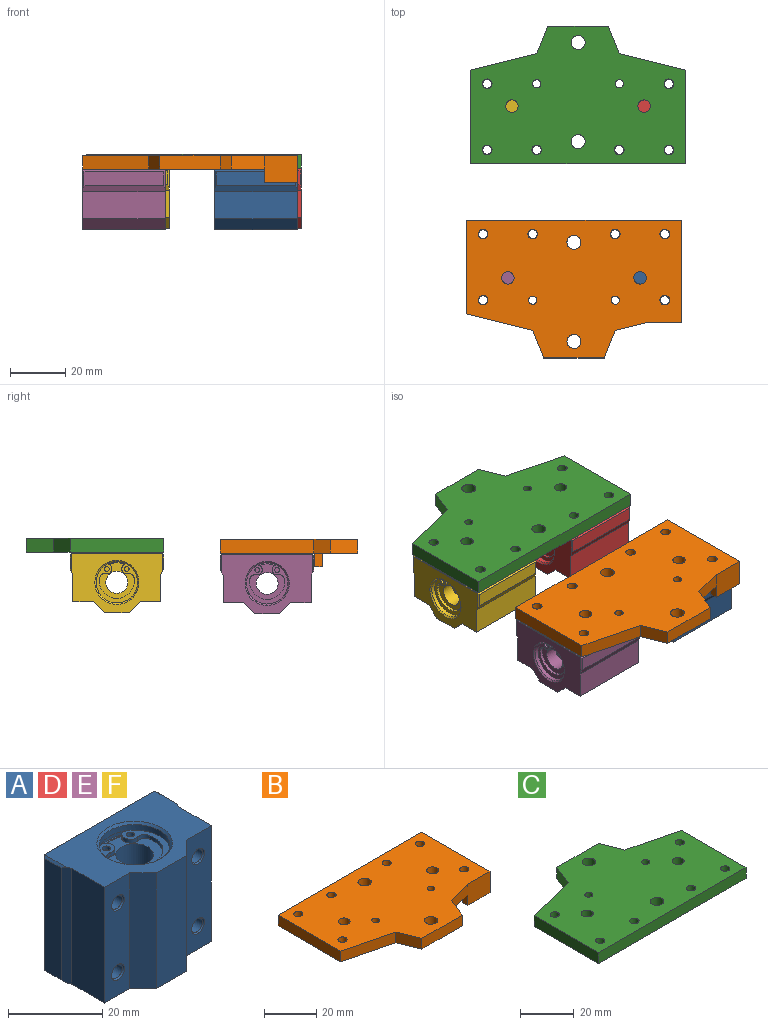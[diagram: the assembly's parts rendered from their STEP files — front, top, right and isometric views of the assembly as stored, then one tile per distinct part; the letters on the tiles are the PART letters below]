
ASSEMBLY  parts=6 mates=4
PART A: 101 faces, bbox 34x22x30 mm
  f0: cylinder r=7.5mm len=15mm, axis (0,0,-1), area 11.8mm2, adj f30,f89
  f1: plane 9.06x1.44mm, normal (0,0,-1), area 2.8mm2, adj f26,f27,f84,f85
  f2: plane 9.06x1.44mm, normal (0,0,1), area 2.8mm2, adj f31,f32,f70,f71
  f3: plane 30x7.5mm, normal (0,-1,0), area 201.6mm2, adj f7,f8,f11,f12,f52,f57
  f4: plane 29x8mm, normal (0,1,0), area 206.9mm2, adj f21,f22,f23,f24,f48,f53
  f5: plane 30x7.5mm, normal (0,-1,0), area 201.6mm2, adj f7,f8,f14,f15,f42,f47
  f6: plane 29x8mm, normal (0,1,0), area 206.9mm2, adj f18,f19,f23,f24,f38,f43
  f7: plane 33x21.5mm, normal (0,0,1), area 418mm2, adj f3,f5,f10,f11,f12,f13,f14,f15
  f8: plane 33x21.5mm, normal (0,0,-1), area 418mm2, adj f3,f5,f10,f11,f12,f13,f14,f15
  f9: plane 29x5mm, normal (-1,0,0), area 145mm2, adj f10,f22,f34,f35
  f10: plane 30x2.14mm, normal (-0.91,-0.42,0), area 70.4mm2, adj f7,f8,f9,f11,f34,f35
  f11: plane 30x9.86mm, normal (-1,0,0), area 295.7mm2, adj f3,f7,f8,f10
  f12: plane 30x4mm, normal (-0.71,-0.71,0), area 169.7mm2, adj f3,f7,f8,f13
  f13: plane 30x9mm, normal (0,-1,0), area 270mm2, adj f7,f8,f12,f14
  f14: plane 30x4mm, normal (0.71,-0.71,0), area 169.7mm2, adj f5,f7,f8,f13
  f15: plane 30x9.86mm, normal (1,0,0), area 295.7mm2, adj f5,f7,f8,f16
  f16: plane 30x2.14mm, normal (0.91,-0.42,0), area 70.4mm2, adj f7,f8,f15,f17,f36,f37
  f17: plane 29x5mm, normal (1,0,0), area 145mm2, adj f16,f18,f36,f37
  f18: plane 30x1mm, normal (0.71,0.71,0), area 41.7mm2, adj f6,f17,f23,f24,f36,f37
  f19: plane 29.8x0.4mm, normal (-0.71,0.71,0), area 16.6mm2, adj f6,f20,f23,f24
  f20: plane 29.8x15.2mm, normal (0,1,0), area 453mm2, adj f19,f21,f23,f24
  f21: plane 29.8x0.4mm, normal (0.71,0.71,0), area 16.6mm2, adj f4,f20,f23,f24
  f22: plane 30x1mm, normal (-0.71,0.71,0), area 41.7mm2, adj f4,f9,f23,f24,f34,f35
  f23: plane 33x0.5mm, normal (0,0.71,-0.71), area 14.2mm2, adj f4,f6,f8,f18,f19,f20,f21,f22
  f24: plane 33x0.5mm, normal (0,0.71,0.71), area 14.2mm2, adj f4,f6,f7,f18,f19,f20,f21,f22
  f25: cone r=8mm half-angle=45deg, axis (0,0,1), area 34.4mm2, adj f7,f26
  f26: cylinder r=7.5mm len=15mm, axis (0,0,-1), area 70.7mm2, adj f1,f25,f92
  f27: cylinder r=7.85mm len=15.7mm, axis (0,0,-1), area 17.1mm2, adj f1,f28,f84,f85,f86
  f28: plane 15.7x15.7mm, normal (0,0,1), area 16.9mm2, adj f27,f29
  f29: cylinder r=7.5mm len=15mm, axis (0,0,-1), area 11.8mm2, adj f28,f87
  f30: plane 15.7x15.7mm, normal (0,0,-1), area 16.9mm2, adj f0,f31
  f31: cylinder r=7.85mm len=15.7mm, axis (0,0,-1), area 17.1mm2, adj f2,f30,f70,f71,f72
  f32: cylinder r=7.5mm len=15mm, axis (0,0,-1), area 70.7mm2, adj f2,f33,f60
  f33: cone r=7.5mm half-angle=45deg, axis (0,0,-1), area 34.4mm2, adj f8,f32
  f34: plane 6.57x0.5mm, normal (-0.71,0,0.71), area 4.1mm2, adj f7,f9,f10,f22
  f35: plane 6.57x0.5mm, normal (-0.71,0,-0.71), area 4.1mm2, adj f8,f9,f10,f22
  f36: plane 6.57x0.5mm, normal (0.71,0,0.71), area 4.1mm2, adj f7,f16,f17,f18
  f37: plane 6.57x0.5mm, normal (0.71,0,-0.71), area 4.1mm2, adj f8,f16,f17,f18
  f38: cone r=2mm half-angle=45deg, axis (0,1,0), area 6.1mm2, adj f6,f39
  f39: cylinder r=1.62mm len=9.62mm, axis (0,-1,0), area 98mm2, adj f38,f40
  f40: plane 3.4x3.4mm, normal (0,-1,0), area 0.8mm2, adj f39,f41
  f41: cylinder r=1.7mm len=7.6mm, axis (0,-1,0), area 81.2mm2, adj f40,f42
  f42: cone r=1.7mm half-angle=30deg, axis (0,-1,0), area 5.3mm2, adj f5,f41
  f43: cone r=2mm half-angle=45deg, axis (0,1,0), area 6.1mm2, adj f6,f44
  f44: cylinder r=1.62mm len=9.62mm, axis (0,-1,0), area 98mm2, adj f43,f45
  f45: plane 3.4x3.4mm, normal (0,-1,0), area 0.8mm2, adj f44,f46
  f46: cylinder r=1.7mm len=7.6mm, axis (0,-1,0), area 81.2mm2, adj f45,f47
  f47: cone r=1.7mm half-angle=30deg, axis (0,-1,0), area 5.3mm2, adj f5,f46
  f48: cone r=2mm half-angle=45deg, axis (0,1,0), area 6.1mm2, adj f4,f49
  f49: cylinder r=1.62mm len=9.62mm, axis (0,-1,0), area 98mm2, adj f48,f50
  f50: plane 3.4x3.4mm, normal (0,-1,0), area 0.8mm2, adj f49,f51
  f51: cylinder r=1.7mm len=7.6mm, axis (0,-1,0), area 81.2mm2, adj f50,f52
  f52: cone r=1.7mm half-angle=30deg, axis (0,-1,0), area 5.3mm2, adj f3,f51
  f53: cone r=2mm half-angle=45deg, axis (0,1,0), area 6.1mm2, adj f4,f54
  f54: cylinder r=1.62mm len=9.62mm, axis (0,-1,0), area 98mm2, adj f53,f55
  f55: plane 3.4x3.4mm, normal (0,-1,0), area 0.8mm2, adj f54,f56
  f56: cylinder r=1.7mm len=7.6mm, axis (0,-1,0), area 81.2mm2, adj f55,f57
  f57: cone r=1.7mm half-angle=30deg, axis (0,-1,0), area 5.3mm2, adj f3,f56
  f58: plane 1.7x1.7mm, normal (0,0,-1), area 2.3mm2, adj f62
  f59: plane 1.7x1.7mm, normal (0,0,-1), area 2.3mm2, adj f63
  f60: plane 15x14.21mm, normal (0,0,-1), area 58.1mm2, adj f32,f61,f62,f63,f64,f65,f66,f67
  f61: plane 1x0.13mm, normal (0.94,0.33,0), area 0.1mm2, adj f60,f64,f71,f91
  f62: cylinder r=0.85mm len=1.7mm, axis (0,0,-1), area 5.3mm2, adj f58,f60
  f63: cylinder r=0.85mm len=1.7mm, axis (0,0,-1), area 5.3mm2, adj f59,f60
  f64: cylinder r=1.8mm len=2.39mm, axis (0,0,-1), area 3.9mm2, adj f60,f61,f65,f91
  f65: cylinder r=1.8mm len=2.2mm, axis (0,0,-1), area 2.9mm2, adj f60,f64,f66,f91
  f66: cylinder r=6.35mm len=12.7mm, axis (0,0,-1), area 22.4mm2, adj f60,f65,f67,f91
  f67: cylinder r=1.8mm len=2.2mm, axis (0,0,-1), area 2.9mm2, adj f60,f66,f68,f91
  f68: cylinder r=1.8mm len=2.39mm, axis (0,0,-1), area 3.9mm2, adj f60,f67,f69,f91
  f69: plane 1x0.13mm, normal (-0.94,0.33,0), area 0.1mm2, adj f60,f68,f70,f91
  f70: cylinder r=1.7mm len=2.59mm, axis (0,0,-1), area 3.1mm2, adj f2,f31,f60,f69,f72,f91
  f71: cylinder r=1.7mm len=2.59mm, axis (0,0,-1), area 3.1mm2, adj f2,f31,f60,f61,f72,f91
  f72: plane 15.7x14.57mm, normal (0,0,1), area 30mm2, adj f31,f70,f71,f89
  f73: plane 1.7x1.7mm, normal (0,0,1), area 2.3mm2, adj f76
  f74: plane 1.7x1.7mm, normal (0,0,1), area 2.3mm2, adj f77
  f75: plane 1x0.13mm, normal (-0.94,0.33,0), area 0.1mm2, adj f78,f85,f90,f92
  f76: cylinder r=0.85mm len=1.7mm, axis (0,0,1), area 5.3mm2, adj f73,f92
  f77: cylinder r=0.85mm len=1.7mm, axis (0,0,1), area 5.3mm2, adj f74,f92
  f78: cylinder r=1.8mm len=2.39mm, axis (0,0,1), area 3.9mm2, adj f75,f79,f90,f92
  f79: cylinder r=1.8mm len=2.2mm, axis (0,0,1), area 2.9mm2, adj f78,f80,f90,f92
  f80: cylinder r=6.35mm len=12.7mm, axis (0,0,1), area 22.4mm2, adj f79,f81,f90,f92
  f81: cylinder r=1.8mm len=2.2mm, axis (0,0,1), area 2.9mm2, adj f80,f82,f90,f92
  f82: cylinder r=1.8mm len=2.39mm, axis (0,0,1), area 3.9mm2, adj f81,f83,f90,f92
  f83: plane 1x0.13mm, normal (0.94,0.33,0), area 0.1mm2, adj f82,f84,f90,f92
  f84: cylinder r=1.7mm len=2.59mm, axis (0,0,1), area 3.1mm2, adj f1,f27,f83,f86,f90,f92
  f85: cylinder r=1.7mm len=2.59mm, axis (0,0,1), area 3.1mm2, adj f1,f27,f75,f86,f90,f92
  f86: plane 15.7x14.57mm, normal (0,0,-1), area 30mm2, adj f27,f84,f85,f87
  f87: torus R=7.1mm, axis (0,0,1), area 29mm2, adj f29,f86,f90
  f88: cylinder r=4mm len=24mm, axis (0,0,1), area 603.2mm2, adj f90,f91
  f89: torus R=7.1mm, axis (0,0,1), area 29mm2, adj f0,f72,f91
  f90: plane 12.95x12.7mm, normal (0,0,1), area 61.3mm2, adj f75,f78,f79,f80,f81,f82,f83,f84
  f91: plane 12.95x12.7mm, normal (0,0,-1), area 61.3mm2, adj f61,f64,f65,f66,f67,f68,f69,f70
  f92: plane 15x14.21mm, normal (0,0,1), area 58.1mm2, adj f26,f75,f76,f77,f78,f79,f80,f81
  f93: plane 15x15mm, normal (0,0,-1), area 16.1mm2, adj f94,f96
  f94: cylinder r=7.15mm len=14.3mm, axis (0,0,1), area 49.4mm2, adj f93,f95
  f95: plane 15x15mm, normal (0,0,1), area 16.1mm2, adj f94,f96
  f96: cylinder r=7.5mm len=15mm, axis (0,0,-1), area 51.8mm2, adj f93,f95
  f97: plane 15x15mm, normal (0,0,-1), area 16.1mm2, adj f98,f100
  f98: cylinder r=7.15mm len=14.3mm, axis (0,0,1), area 49.4mm2, adj f97,f99
  f99: plane 15x15mm, normal (0,0,1), area 16.1mm2, adj f98,f100
  f100: cylinder r=7.5mm len=15mm, axis (0,0,-1), area 51.8mm2, adj f97,f99
PART B: 26 faces, bbox 78x50x10 mm
  f0: plane 12x5mm, normal (0.24,-0.97,0), area 61.8mm2, adj f2,f20,f21,f22
  f1: plane 37x10mm, normal (1,0,0), area 199mm2, adj f7,f20,f21,f22,f24,f25
  f2: plane 10x5mm, normal (0.93,-0.37,0), area 53.9mm2, adj f0,f3,f20,f21
  f3: plane 22x5mm, normal (0,-1,0), area 110mm2, adj f2,f4,f20,f21
  f4: plane 10x5mm, normal (-0.93,-0.37,0), area 53.9mm2, adj f3,f5,f20,f21
  f5: plane 24x6mm, normal (-0.24,-0.97,0), area 123.7mm2, adj f4,f6,f20,f21
  f6: plane 34x5mm, normal (-1,0,0), area 170mm2, adj f5,f7,f20,f21
  f7: plane 78x5mm, normal (0,1,0), area 390mm2, adj f1,f6,f20,f21
  f8: cylinder r=1.75mm len=5mm, axis (0,0,-1), area 55mm2, adj f20,f21
  f9: cylinder r=1.75mm len=5mm, axis (0,0,-1), area 55mm2, adj f20,f21
  f10: cylinder r=1.75mm len=5mm, axis (0,0,-1), area 55mm2, adj f20,f21
  f11: cylinder r=1.75mm len=5mm, axis (0,0,-1), area 55mm2, adj f20,f21
  f12: cylinder r=1.5mm len=5mm, axis (0,0,-1), area 47.1mm2, adj f20,f21
  f13: cylinder r=1.75mm len=5mm, axis (0,0,-1), area 55mm2, adj f20,f21
  f14: cylinder r=1.5mm len=5mm, axis (0,0,-1), area 47.1mm2, adj f20,f21
  f15: cylinder r=1.75mm len=5mm, axis (0,0,-1), area 55mm2, adj f20,f21
  f16: cylinder r=2.55mm len=5.1mm, axis (0,0,-1), area 80.1mm2, adj f20,f21
  f17: cylinder r=2.25mm len=5mm, axis (0,0,-1), area 70.7mm2, adj f20,f21
  f18: cylinder r=2.25mm len=5mm, axis (0,0,-1), area 70.7mm2, adj f20,f21
  f19: cylinder r=2.55mm len=5.1mm, axis (0,0,-1), area 80.1mm2, adj f20,f21
  f20: plane 78x50mm, normal (0,0,1), area 3109.5mm2, adj f0,f1,f2,f3,f4,f5,f6,f7
  f21: plane 78x50mm, normal (0,0,-1), area 3075.9mm2, adj f0,f1,f2,f3,f4,f5,f6,f7
  f22: plane 12x10mm, normal (0,-1,0), area 120mm2, adj f0,f1,f20,f23,f25
  f23: plane 5x2.8mm, normal (-1,0,0), area 14mm2, adj f21,f22,f24,f25
  f24: plane 12x5mm, normal (0,1,0), area 60mm2, adj f1,f21,f23,f25
  f25: plane 12x2.8mm, normal (0,0,-1), area 33.6mm2, adj f1,f22,f23,f24
PART C: 22 faces, bbox 78x50x5 mm
  f0: plane 34x5mm, normal (1,0,0), area 170mm2, adj f1,f7,f20,f21
  f1: plane 24x6mm, normal (0.24,0.97,0), area 123.7mm2, adj f0,f2,f20,f21
  f2: plane 10x5mm, normal (0.93,0.37,0), area 53.9mm2, adj f1,f3,f20,f21
  f3: plane 22x5mm, normal (0,1,0), area 110mm2, adj f2,f4,f20,f21
  f4: plane 10x5mm, normal (-0.93,0.37,0), area 53.9mm2, adj f3,f5,f20,f21
  f5: plane 24x6mm, normal (-0.24,0.97,0), area 123.7mm2, adj f4,f6,f20,f21
  f6: plane 34x5mm, normal (-1,0,0), area 170mm2, adj f5,f7,f20,f21
  f7: plane 78x5mm, normal (0,-1,0), area 390mm2, adj f0,f6,f20,f21
  f8: cylinder r=1.75mm len=5mm, axis (0,0,-1), area 55mm2, adj f20,f21
  f9: cylinder r=1.75mm len=5mm, axis (0,0,-1), area 55mm2, adj f20,f21
  f10: cylinder r=1.75mm len=5mm, axis (0,0,-1), area 55mm2, adj f20,f21
  f11: cylinder r=1.75mm len=5mm, axis (0,0,-1), area 55mm2, adj f20,f21
  f12: cylinder r=1.5mm len=5mm, axis (0,0,-1), area 47.1mm2, adj f20,f21
  f13: cylinder r=1.75mm len=5mm, axis (0,0,-1), area 55mm2, adj f20,f21
  f14: cylinder r=1.5mm len=5mm, axis (0,0,-1), area 47.1mm2, adj f20,f21
  f15: cylinder r=1.75mm len=5mm, axis (0,0,-1), area 55mm2, adj f20,f21
  f16: cylinder r=2.55mm len=5.1mm, axis (0,0,-1), area 80.1mm2, adj f20,f21
  f17: cylinder r=2.25mm len=5mm, axis (0,0,-1), area 70.7mm2, adj f20,f21
  f18: cylinder r=2.25mm len=5mm, axis (0,0,-1), area 70.7mm2, adj f20,f21
  f19: cylinder r=2.55mm len=5.1mm, axis (0,0,-1), area 80.1mm2, adj f20,f21
  f20: plane 78x50mm, normal (0,0,1), area 3091.5mm2, adj f0,f1,f2,f3,f4,f5,f6,f7
  f21: plane 78x50mm, normal (0,0,-1), area 3091.5mm2, adj f0,f1,f2,f3,f4,f5,f6,f7
PART D: same geometry as A
PART E: same geometry as A
PART F: same geometry as A
PLACE A rot(axis=(0.58,0.58,0.58),120deg) t=(7.52,-54.61,-11.38)mm
PLACE B t=(-1.48,-20.61,-0.38)mm
PLACE C at identity fixed
PLACE D rot(axis=(0.58,0.58,0.58),120deg) t=(9,0,-11)mm
PLACE E rot(axis=(0.58,0.58,0.58),120deg) t=(-40.48,-54.61,-11.38)mm
PLACE F rot(axis=(0.58,0.58,0.58),120deg) t=(-39,0,-11)mm
MATE fastened A.f53 <-> B.f8  axis (0,0,1) through (31.52,-66.61,-0.38)mm
MATE fastened E.f48 <-> B.f11  axis (0,0,1) through (-34.48,-66.61,-0.38)mm
MATE fastened F.f53 <-> C.f13  axis (0,0,1) through (-15,-12,0)mm
MATE fastened D.f53 <-> C.f9  axis (0,0,1) through (33,-12,0)mm
